# Revit family: Panel_Shower-Behavioral_Safety_Products-SV715
name_source: partatom
category: Plumbing Fixtures
revit_build: Autodesk Revit 2018 (Build: 20190510_1515(x64)
units: mm (PartAtom-declared; Revit-internal decimal feet)

## family parameters
Cut with Voids When Loaded = No
Host = Face
OmniClass Number = 23.40.20.21
OmniClass Title = Toilet and Bath Specialties
Part Type = Normal
Room Calculation Point = No
Round Connector Dimension = Use Diameter
Shared = No

## types (1)
- Standard
    Default Elevation = 0"
    Depth = 42"
    Description = Ligature Resistant Shower Panel
    Front Panel = Metal - Behavioral Safety - White powder coat
    Height = 40"
    Inlet Supplies = Metal - Behavioral Safety - Chrome
    Manufacturer = Behavioral Safety Products
    Manufacturer Fax = 706-705-1191
    Model = SV715
    Product Brochure URL = http://besafeprod.com
    Product Documentation Link = http://besafeprod.com
    Product Page URL = http://besafeprod.com
    Revit Object Download Link = http://library.smartbim.com
    Shower = Metal - Behavioral Safety - Chrome
    URL = http://besafeprod.com
    Valve Trim = Metal - Behavioral Safety - Chrome
    Width = 9 3/8"
    aaa = 42"

## geometry (parser evidence)
native form markers: Blend x12, Sweep x13
no freeform markers — native parametric forms only
